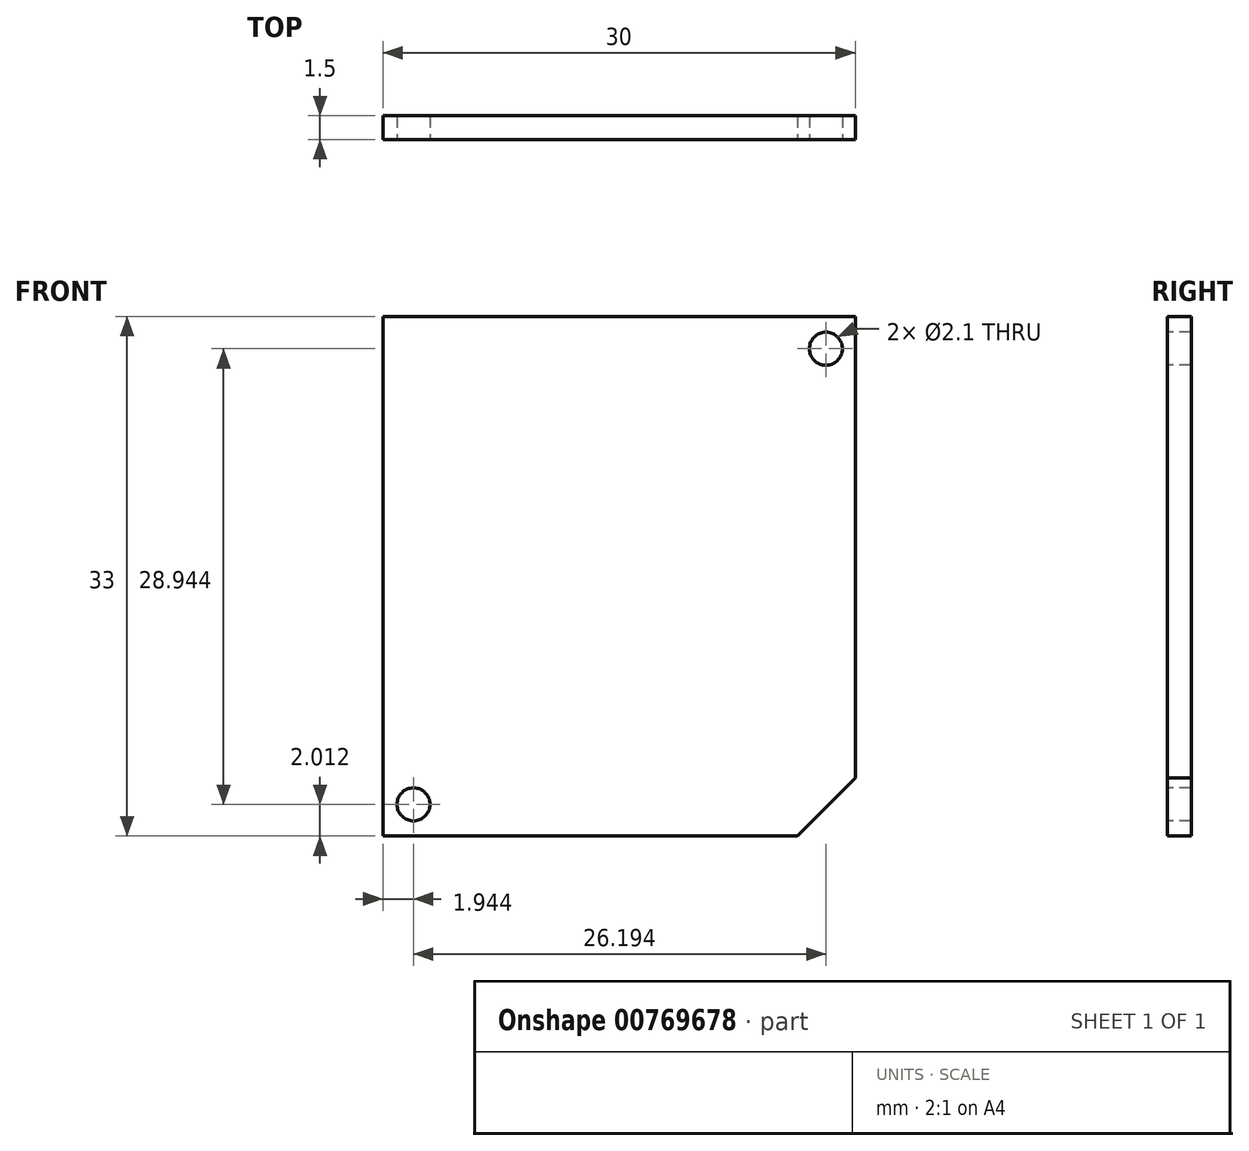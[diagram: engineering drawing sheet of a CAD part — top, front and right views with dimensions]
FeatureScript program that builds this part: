
annotation { "Feature Type Name" : "Feature", "Feature Type Description" : "" }
export const myFeature = defineFeature(function(context is Context, id is Id, definition is map)
    precondition{}
    {
        {
            var Q0;
            Q0=qCreatedBy(makeId("Front.planeOp"),FACE);
            var sketch = newSketch(context, id + "F0", { "sketchPlane" : qUnion([Q0])});
            skLineSegment(sketch, "E0", {"start": v(14.53, 20.21) * mm, "end": v(14.53, -11.48) * mm});
            skLineSegment(sketch, "E1", {"start": v(-18.47, 20.21) * mm, "end": v(14.53, 20.21) * mm});
            skLineSegment(sketch, "E2", {"start": v(-18.47, 20.21) * mm, "end": v(-18.47, -15.79) * mm});
            skLineSegment(sketch, "E3", {"start": v(-18.47, -15.79) * mm, "end": v(10.23, -15.79) * mm});
            skLineSegment(sketch, "E4", {"start": v(10.23, -15.79) * mm, "end": v(14.53, -11.48) * mm});
            skLineSegment(sketch, "E5", {"start": v(13.03, 18.71) * mm, "end": v(-16.97, 18.71) * mm});
            skLineSegment(sketch, "E6", {"start": v(-16.97, 18.71) * mm, "end": v(-16.97, -14.29) * mm});
            skLineSegment(sketch, "E7", {"start": v(-16.97, -14.29) * mm, "end": v(9.36, -14.29) * mm});
            skLineSegment(sketch, "E8", {"start": v(9.36, -14.29) * mm, "end": v(13.03, -10.61) * mm});
            skLineSegment(sketch, "E9", {"start": v(13.03, -10.61) * mm, "end": v(13.03, 18.71) * mm});
            skCircle(sketch, "E10", {"center": v(11.17, 16.67) * mm, "radius": 1.05 * mm});
            skCircle(sketch, "E11", {"center": v(-15.03, -12.28) * mm, "radius": 1.05 * mm});
            skSolve(sketch);
        }
        {
            var Q0;
            Q0=makeQuery(id+"F0.imprint","IMPRINT",FACE,{"disambiguationData":[TD([[makeQuery(id+"F0.imprint","IMPRINT",EDGE,{"derivedFrom":sQuery(id+"F0.wireOp",EDGE,"E5")}),1.0]])]});
            extrude(context, id + "F1", {"entities" : qUnion([Q0]), "oppositeDirection" : true, "depth" : 1.5 * mm, "offsetDistance" : 25 * mm});
        }
    });
